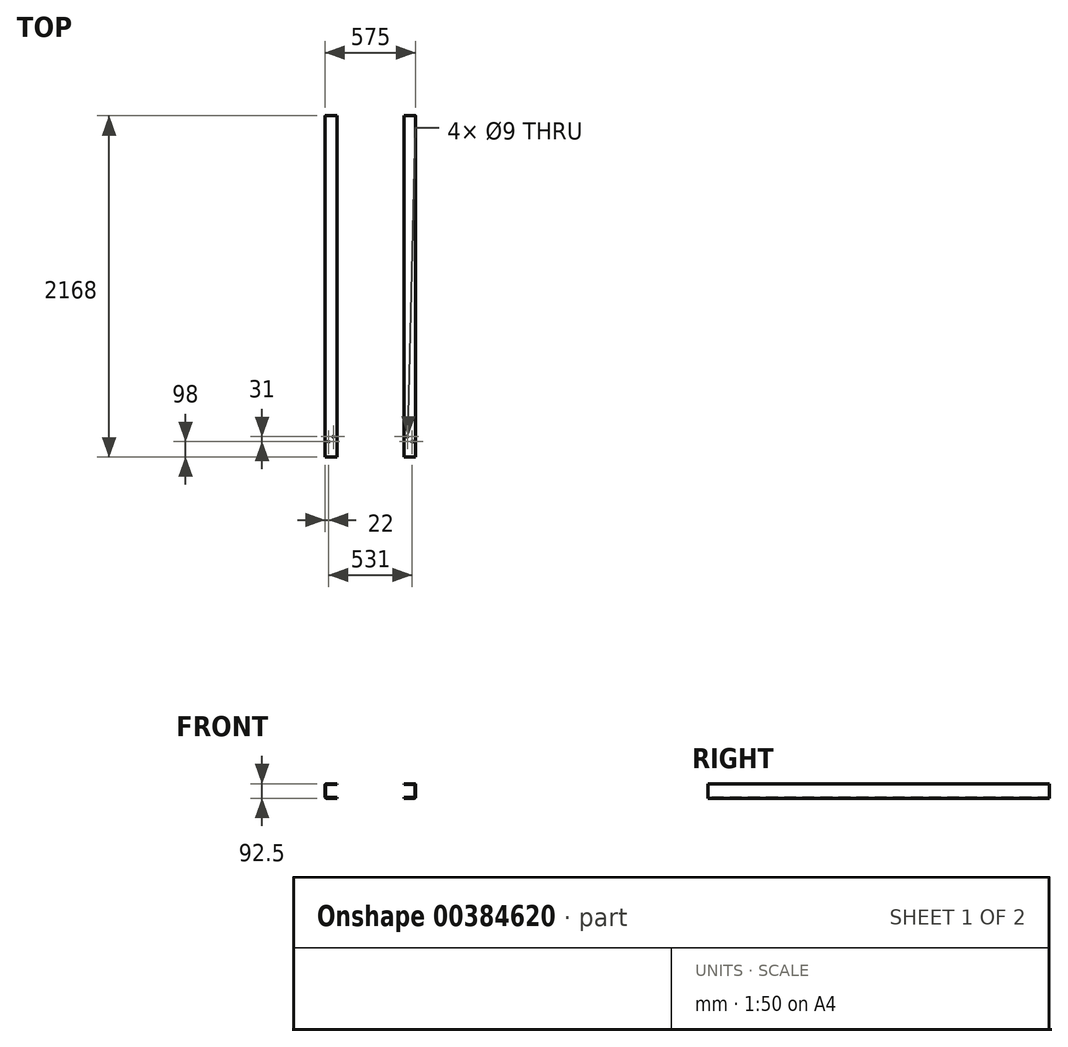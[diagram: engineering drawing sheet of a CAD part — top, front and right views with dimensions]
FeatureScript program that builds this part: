
annotation { "Feature Type Name" : "Feature", "Feature Type Description" : "" }
export const myFeature = defineFeature(function(context is Context, id is Id, definition is map)
    precondition{}
    {
        {
            var Q0;
            Q0=qCreatedBy(makeId("Front.planeOp"),FACE);
            var sketch = newSketch(context, id + "F0", { "sketchPlane" : qUnion([Q0])});
            skLineSegment(sketch, "E0.bottom", {"start": v(-37.5, -46.25) * mm, "end": v(29.5, -46.25) * mm});
            skLineSegment(sketch, "E0.top", {"start": v(-37.5, 46.25) * mm, "end": v(29.5, 46.25) * mm});
            skLineSegment(sketch, "E0.left", {"start": v(-37.5, -46.25) * mm, "end": v(-37.5, -42.25) * mm});
            skLineSegment(sketch, "E0.right", {"start": v(37.5, -38.25) * mm, "end": v(37.5, 38.25) * mm});
            skPoint(sketch, "E0.middle", {"position": v(0, 0) * mm});
            skLineSegment(sketch, "E1", {"start": v(-37.5, 42.25) * mm, "end": v(29.5, 42.25) * mm});
            skLineSegment(sketch, "E2", {"start": v(33.5, 38.25) * mm, "end": v(33.5, -38.25) * mm});
            skLineSegment(sketch, "E3", {"start": v(29.5, -42.25) * mm, "end": v(-37.5, -42.25) * mm});
            skLineSegment(sketch, "E4.trimOffspring", {"start": v(-37.5, 42.25) * mm, "end": v(-37.5, 46.25) * mm});
            skPoint(sketch, "E5.visualSharp", {"position": v(33.5, 42.25) * mm});
            skArc(sketch, "E5.filletArc", {"start": v(33.5, 38.25) * mm, "mid": v(32.33, 41.08) * mm, "end": v(29.5, 42.25) * mm});
            skPoint(sketch, "E6.visualSharp", {"position": v(33.5, -42.25) * mm});
            skArc(sketch, "E6.filletArc", {"start": v(29.5, -42.25) * mm, "mid": v(32.33, -41.08) * mm, "end": v(33.5, -38.25) * mm});
            skPoint(sketch, "E7.visualSharp", {"position": v(37.5, 46.25) * mm});
            skArc(sketch, "E7.filletArc", {"start": v(37.5, 38.25) * mm, "mid": v(35.16, 43.9) * mm, "end": v(29.5, 46.25) * mm});
            skPoint(sketch, "E8.visualSharp", {"position": v(37.5, -46.25) * mm});
            skArc(sketch, "E8.filletArc", {"start": v(29.5, -46.25) * mm, "mid": v(35.16, -43.9) * mm, "end": v(37.5, -38.25) * mm});
            skSolve(sketch);
        }
        {
            var Q0;
            Q0=qSketchRegion(id+"F0",true);
            extrude(context, id + "F1", {"entities" : qUnion([Q0]), "oppositeDirection" : true, "depth" : 2168 * mm});
        }
        {
            var Q0;
            Q0=qCreatedBy(makeId("Top.planeOp"),FACE);
            var Q1;
            Q1=qBodyType(qCreatedBy(id+"FbHpdg401B42YHa",EDGE),BodyType.WIRE);
            cPlane(context, id + "F2", {"entities" : qUnion([Q0, Q1]), "cplaneType" : CPlaneType.OFFSET, "offset" : 46.25 * mm, "width" : 150 * mm, "height" : 150 * mm});
        }
        {
            var Q0;
            Q0=qCreatedBy(id+"F2.planeOp",FACE);
            var sketch = newSketch(context, id + "F3", { "sketchPlane" : qUnion([Q0])});
            skLineSegment(sketch, "E9", {"start": v(0, 0) * mm, "end": v(0, 83.5) * mm});
            skLineSegment(sketch, "E10", {"start": v(-41.75, 0) * mm, "end": v(0, 0) * mm});
            skLineSegment(sketch, "E11", {"start": v(41.75, 0) * mm, "end": v(0, 0) * mm});
            skLineSegment(sketch, "E12", {"start": v(0, 83.5) * mm, "end": v(0, 158) * mm});
            skLineSegment(sketch, "E13.bottom", {"start": v(-37.5, 83.5) * mm, "end": v(37.5, 83.5) * mm});
            skLineSegment(sketch, "E13.top", {"start": v(-37.5, -83.5) * mm, "end": v(37.5, -83.5) * mm});
            skLineSegment(sketch, "E13.left", {"start": v(-37.5, 83.5) * mm, "end": v(-37.5, -83.5) * mm});
            skLineSegment(sketch, "E13.right", {"start": v(37.5, 83.5) * mm, "end": v(37.5, -83.5) * mm});
            skPoint(sketch, "E13.middle", {"position": v(0, 0) * mm});
            skLineSegment(sketch, "E14.bottom", {"start": v(-15.5, 129) * mm, "end": v(15.5, 129) * mm});
            skLineSegment(sketch, "E14.top", {"start": v(-15.5, 98) * mm, "end": v(15.5, 98) * mm});
            skLineSegment(sketch, "E14.left", {"start": v(-15.5, 129) * mm, "end": v(-15.5, 98) * mm});
            skLineSegment(sketch, "E14.right", {"start": v(15.5, 129) * mm, "end": v(15.5, 98) * mm});
            skPoint(sketch, "E14.middle", {"position": v(0, 113.5) * mm});
            skCircle(sketch, "E15", {"center": v(15.5, 98) * mm, "radius": 4.5 * mm});
            skCircle(sketch, "E16", {"center": v(-15.5, 129) * mm, "radius": 4.5 * mm});
            skSolve(sketch);
        }
        {
            var Q0;
            {var subQ0=sQuery(id+"F3.wireOp",EDGE,"E14.left");var subQ1=sQuery(id+"F3.wireOp",EDGE,"E14.bottom");var subQ2=makeQuery(id+"F3.imprint","INTERSECT",VERTEX,{"derivedFrom":[subQ1,subQ0]});Q0=makeQuery(id+"F3.imprint","IMPRINT",FACE,{"disambiguationData":[TD([[makeQuery(id+"F3.imprint","IMPRINT",EDGE,{"disambiguationData":[TD([[subQ2,-1.0]])],"derivedFrom":subQ1}),1.0]])]});}
            var Q1;
            {var subQ0=sQuery(id+"F3.wireOp",EDGE,"E14.left");var subQ1=sQuery(id+"F3.wireOp",EDGE,"E14.bottom");var subQ2=makeQuery(id+"F3.imprint","INTERSECT",VERTEX,{"derivedFrom":[subQ1,subQ0]});Q1=makeQuery(id+"F3.imprint","IMPRINT",FACE,{"disambiguationData":[TD([[makeQuery(id+"F3.imprint","IMPRINT",EDGE,{"disambiguationData":[TD([[subQ2,-1.0]])],"derivedFrom":subQ1}),-1.0]])]});}
            var Q2;
            {var subQ0=sQuery(id+"F3.wireOp",EDGE,"E14.right");var subQ1=sQuery(id+"F3.wireOp",EDGE,"E14.top");var subQ2=makeQuery(id+"F3.imprint","INTERSECT",VERTEX,{"derivedFrom":[subQ1,subQ0]});Q2=makeQuery(id+"F3.imprint","IMPRINT",FACE,{"disambiguationData":[TD([[makeQuery(id+"F3.imprint","IMPRINT",EDGE,{"disambiguationData":[TD([[subQ2,1.0]])],"derivedFrom":subQ1}),1.0]])]});}
            var Q3;
            {var subQ0=sQuery(id+"F3.wireOp",EDGE,"E14.right");var subQ1=sQuery(id+"F3.wireOp",EDGE,"E14.top");var subQ2=makeQuery(id+"F3.imprint","INTERSECT",VERTEX,{"derivedFrom":[subQ1,subQ0]});Q3=makeQuery(id+"F3.imprint","IMPRINT",FACE,{"disambiguationData":[TD([[makeQuery(id+"F3.imprint","IMPRINT",EDGE,{"disambiguationData":[TD([[subQ2,1.0]])],"derivedFrom":subQ1}),-1.0]])]});}
            extrude(context, id + "F4", {"entities" : qUnion([Q0, Q1, Q2, Q3]), "operationType" : NewBodyOperationType.REMOVE, "endBound" : BoundingType.UP_TO_NEXT, "oppositeDirection" : true, "depth" : 25 * mm});
        }
        {
            var Q0;
            Q0=qCreatedBy(makeId("Right.planeOp"),FACE);
            cPlane(context, id + "F5", {"entities" : qUnion([Q0]), "cplaneType" : CPlaneType.OFFSET, "offset" : 250 * mm, "oppositeDirection" : true, "width" : 150 * mm, "height" : 150 * mm});
        }
        {
            var Q0;
            Q0=makeQuery(id+"F1.opExtrude","SWEPT_BODY",BODY,{"disambiguationData":[OSD([sQuery(id+"F0.wireOp",EDGE,"E0.bottom"),sQuery(id+"F0.wireOp",EDGE,"E0.top"),sQuery(id+"F0.wireOp",EDGE,"E0.left"),sQuery(id+"F0.wireOp",EDGE,"E0.right"),sQuery(id+"F0.wireOp",EDGE,"E1"),sQuery(id+"F0.wireOp",EDGE,"E2"),sQuery(id+"F0.wireOp",EDGE,"E3"),sQuery(id+"F0.wireOp",EDGE,"E4.trimOffspring"),sQuery(id+"F0.wireOp",EDGE,"E5.filletArc"),sQuery(id+"F0.wireOp",EDGE,"E6.filletArc"),sQuery(id+"F0.wireOp",EDGE,"E7.filletArc"),sQuery(id+"F0.wireOp",EDGE,"E8.filletArc")])]});
            var Q1;
            Q1=qCreatedBy(id+"F5.planeOp",FACE);
            mirror(context, id + "F6", {"entities" : qUnion([Q0]), "mirrorPlane" : qUnion([Q1])});
        }
    });
